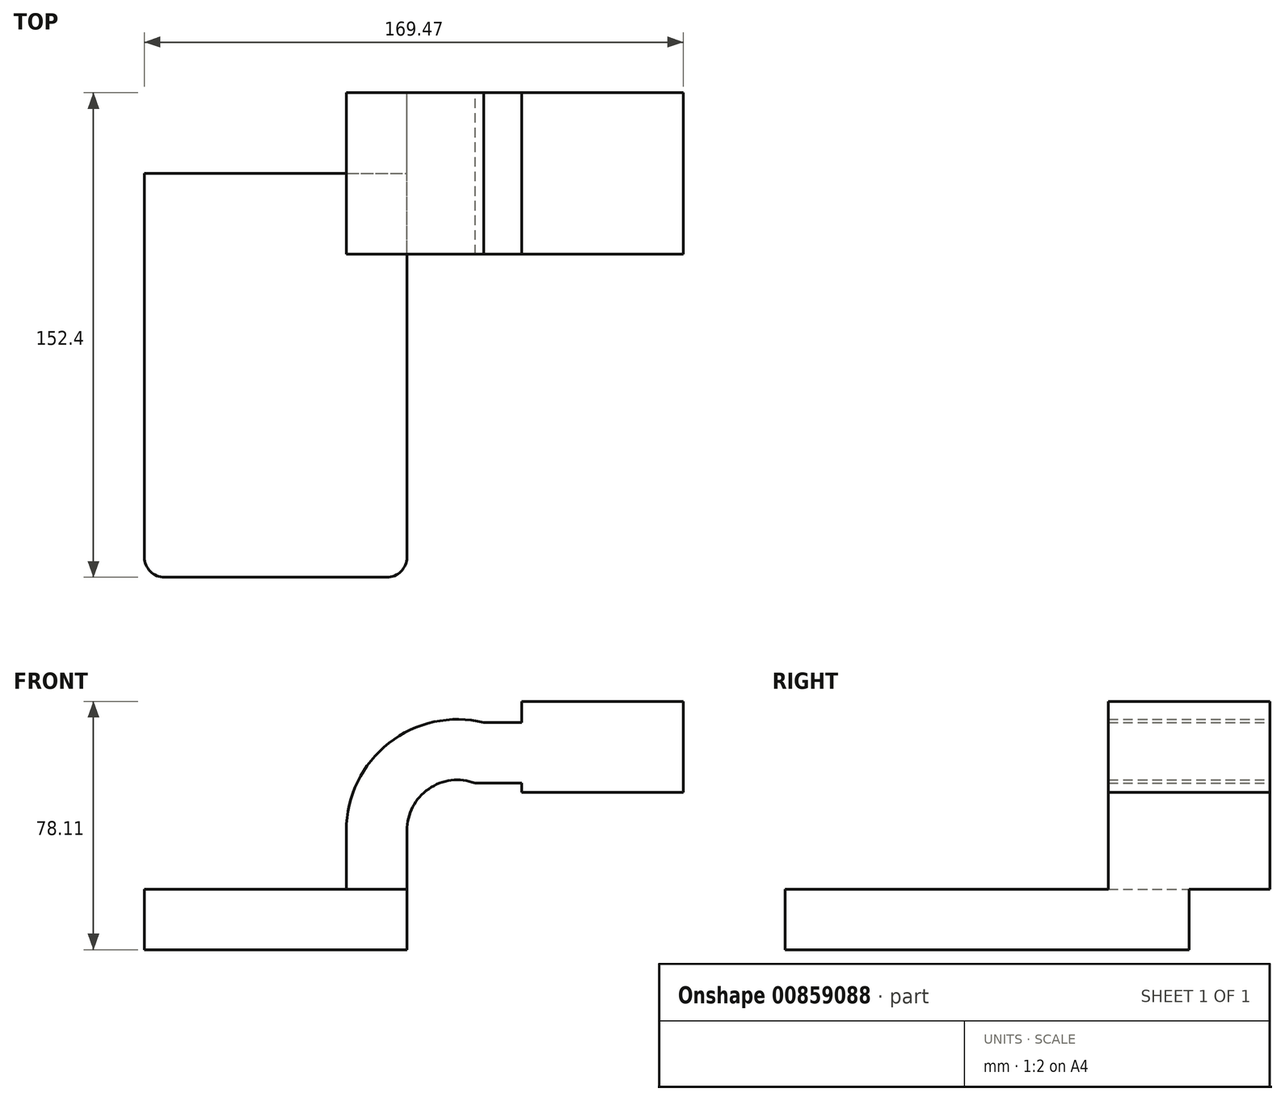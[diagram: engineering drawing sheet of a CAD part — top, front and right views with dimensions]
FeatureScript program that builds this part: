
annotation { "Feature Type Name" : "Feature", "Feature Type Description" : "" }
export const myFeature = defineFeature(function(context is Context, id is Id, definition is map)
    precondition{}
    {
        {
            var Q0;
            Q0=qCreatedBy(makeId("Front.planeOp"),FACE);
            var sketch = newSketch(context, id + "F0", { "sketchPlane" : qUnion([Q0])});
            skLineSegment(sketch, "E0.bottom", {"start": v(-41.28, -9.52) * mm, "end": v(41.28, -9.52) * mm});
            skLineSegment(sketch, "E0.top", {"start": v(-41.28, 9.53) * mm, "end": v(41.27, 9.53) * mm});
            skLineSegment(sketch, "E0.left", {"start": v(-41.27, -9.52) * mm, "end": v(-41.28, 9.53) * mm});
            skLineSegment(sketch, "E0.right", {"start": v(41.28, -9.52) * mm, "end": v(41.27, 9.53) * mm});
            skPoint(sketch, "E0.middle", {"position": v(0, 0) * mm});
            skLineSegment(sketch, "E1.bottom", {"start": v(77.4, 40) * mm, "end": v(128.2, 40) * mm});
            skLineSegment(sketch, "E1.top", {"start": v(77.4, 68.58) * mm, "end": v(128.2, 68.58) * mm});
            skLineSegment(sketch, "E1.left", {"start": v(77.4, 40) * mm, "end": v(77.4, 68.58) * mm});
            skLineSegment(sketch, "E1.right", {"start": v(128.2, 40) * mm, "end": v(128.2, 68.58) * mm});
            skPoint(sketch, "E1.middle", {"position": v(102.8, 54.3) * mm});
            skPoint(sketch, "E2.endSnap0", {"position": v(102.8, 40) * mm});
            skLineSegment(sketch, "E3", {"start": v(41.27, 9.53) * mm, "end": v(41.27, 28) * mm});
            skArc(sketch, "E4", {"start": v(41.27, 28) * mm, "mid": v(48.08, 41.02) * mm, "end": v(62.67, 42.88) * mm});
            skPoint(sketch, "E5.endSnap0", {"position": v(48.08, 41.02) * mm});
            skLineSegment(sketch, "E6", {"start": v(62.67, 42.88) * mm, "end": v(105.23, 42.88) * mm});
            skLineSegment(sketch, "E7.0", {"start": v(65.41, 61.93) * mm, "end": v(105.23, 61.93) * mm});
            skArc(sketch, "E7.1", {"start": v(22.22, 28) * mm, "mid": v(35.57, 55.45) * mm, "end": v(65.41, 61.93) * mm});
            skLineSegment(sketch, "E7.2", {"start": v(22.22, 9.53) * mm, "end": v(22.22, 28) * mm});
            skFitSpline(sketch, "E8", {"points": [v(-41.28, 9.53) * mm, v(77.4, 68.58) * mm], "startDerivative": vector(46.03, 118.1) * mm, "endDerivative": vector(117.13, -34.53) * mm});
            skSolve(sketch);
        }
        {
            var Q0;
            Q0=makeQuery(id+"F0.imprint","IMPRINT",FACE,{"disambiguationData":[TD([[makeQuery(id+"F0.imprint","IMPRINT",EDGE,{"derivedFrom":sQuery(id+"F0.wireOp",EDGE,"E0.bottom")}),1.0]])]});
            extrude(context, id + "F1", {"entities" : qUnion([Q0]), "depth" : 127 * mm, "offsetDistance" : 25.4 * mm});
        }
        {
            var Q0;
            {var subQ0=sQuery(id+"F0.wireOp",EDGE,"E3");Q0=makeQuery(id+"F0.imprint","IMPRINT",FACE,{"disambiguationData":[TD([[makeQuery(id+"F0.imprint","IMPRINT",EDGE,{"derivedFrom":subQ0}),1.0]])]});}
            var Q1;
            {var subQ3=sQuery(id+"F0.wireOp",EDGE,"E1.bottom");Q1=makeQuery(id+"F0.imprint","IMPRINT",FACE,{"disambiguationData":[TD([[makeQuery(id+"F0.imprint","IMPRINT",EDGE,{"derivedFrom":subQ3}),1.0]])]});}
            extrude(context, id + "F2", {"entities" : qUnion([Q0, Q1]), "operationType" : NewBodyOperationType.ADD, "endBound" : BoundingType.SYMMETRIC, "depth" : 50.8 * mm, "offsetDistance" : 25.4 * mm});
        }
        {
            var Q0;
            {var subQ0=sQuery(id+"F0.wireOp",EDGE,"E7.1");Q0=makeQuery(id+"F0.imprint","IMPRINT",FACE,{"disambiguationData":[TD([[makeQuery(id+"F0.imprint","IMPRINT",EDGE,{"derivedFrom":subQ0}),1.0]])]});}
            extrude(context, id + "F3", {"entities" : qUnion([Q0]), "operationType" : NewBodyOperationType.ADD, "endBound" : BoundingType.SYMMETRIC, "depth" : 15.88 * mm, "offsetDistance" : 25.4 * mm});
        }
        {
            var Q0;
            Q0=makeQuery(id+"F1.opExtrude","CAP_EDGE",EDGE,{"disambiguationData":[OSD([sQuery(id+"F0.wireOp",EDGE,"E0.left")])],"isStart":false});
            var Q1;
            Q1=makeQuery(id+"F1.opExtrude","CAP_EDGE",EDGE,{"disambiguationData":[OSD([sQuery(id+"F0.wireOp",EDGE,"E0.right")])],"isStart":false});
            fillet(context, id + "F4", {"entities" : qUnion([Q0, Q1]), "radius" : 6.35 * mm, "tangentPropagation" : true, "allowEdgeOverflow" : false});
        }
    });
